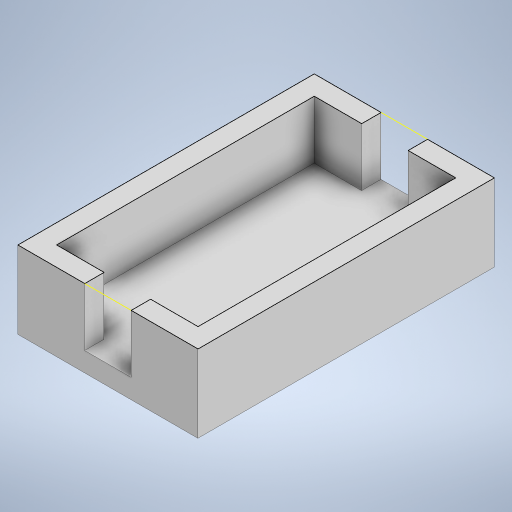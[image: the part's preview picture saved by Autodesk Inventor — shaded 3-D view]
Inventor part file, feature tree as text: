
AUTODESK INVENTOR PART (.ipt)
format: ipt  version: 2024 (Build 280153000, 153)  size: 256,512 bytes
history: native  units: in
note: dims shown in document units (in); Inventor stores cm internally (conversion verified against a paired STEP export)
features: sketch x3, extrude x2
ambient origin geometry x8: Origin, YZ Plane, XZ Plane, XY Plane, X Axis, Y Axis, Z Axis, Center Point
bodies: Solid1 (feature_tree)
feature tree (5):
  extrude  "Extrusion1"  Depth=2.6181in
  extrude  "Extrusion2"  Depth=0.1969in
  sketch  "Sketch3"  dims[d4=0.2362in d5=0.4724in d6=0.4724in d7=0.5906in d8=0.0in d9=0.1969in d10=0.0in]
  sketch  "Sketch1"  dims[d0=1.437in d1=2.6181in]
  sketch  "Sketch2"  dims[d2=0.1969in d3=0.2362in]
